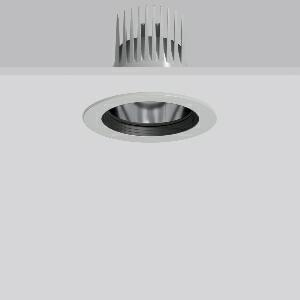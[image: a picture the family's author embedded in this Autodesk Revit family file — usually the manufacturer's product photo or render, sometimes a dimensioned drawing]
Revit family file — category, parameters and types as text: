
# Revit family: heledon_maxi_e_901764_004_3_76_aa6f
name_source: partatom
category: Lighting Fixtures
units: mm (PartAtom-declared; Revit-internal decimal feet)

## family parameters
Cut with Voids When Loaded = No
Host = Face
Light Source = No
Part Type = Normal
Room Calculation Point = No
Round Connector Dimension = Use Diameter
Shared = No

## types (1)
- HELEDON maxi E (1 x LED Modul 935, 4350 lm, 3500)
    Apparent Load = 35 VA
    Approval mark = CE
    CIE Flux Codes = 100 100 100 100 100
    Color Rendering = 92
    Color Temperature = 3500
    Default Elevation = 1800 mm
    Description = Series: HELEDON maxi
Round recessed downlight. Housing: die-cast aluminium, powder-coated. Black plastic ring and recessed LED to prevent glare from the side. Optical assembly with reflector made of MIRO-Silver with 98% total light reflection for outstanding efficiency - can be changed without tools. Best colour rendering index Ra>90. Suitable for Recessed ceiling mounting. Installation without tools thanks to spring fastening system. Including separate LED converter with connecting cable 600 mm.High quality converter without flickering and stroboscopic effect. Through-wiring box (5 pole) available as accessory. The following accessories can be mounted without use of tools: interchangeable lenses, decorative glasses, honeycomb louvre, clear and frosted diffusers, white interchangeable plastic ring. 
Colour: silver
Diameter: 162 mm
Height: 3 mm
Cut-out diameter: 152 mm
Recess height: 200 mm
Luminaire: recess height: 135 mm
Lamp: LED
Socket: without socket
Colour temperature: 3500K
Colour rendering index (CRI): 92
System power: 35 W
Rated luminous flux: 4350 lm
Luminous efficiency: 124 lm/W
Control gear: Converter, dimmable, DALI
Protection class: II
Type of protection: IP 20
    Height = 0 mm  [stored 0 ft]
    Lamp = 1 x LED Modul 935
    Lamp Light Flux = 4350 lm
    Lamp count = 1
    Length = 162 mm
    Lifetime = 50000 h
    Luminous efficacy = 124 lm/W
    Manufacturer = RZB
    ModVariant = No
    Model = 901764.004.3.76
    Mounting Place = Ceiling
    Mounting Type = Recessed
    Number of Poles = 1
    OnlyDefault = Yes
    Power Factor = 1
    Product Name = HELEDON maxi E
    Product group = Recessed downlights
    ProductGroupID = 402
    Protection Class = Protection class II
    Protection Degree = IP 20
    RLX_Detail_Level = 1
    RLX_Emergency_Light_Flux = 0 lm
    RLX_Emergency_Type = 0
    RLX_Emergency_Type_DB = No
    RlxData = <blob elided: 119553 chars, md5=b64f9aeb>
    Socket = socket
    Standby Power = 0 W
    System Light Flux = 4350 lm
    System Power = 35 W
    Type Comments = Product without accessories
    Type Image = 901662.004.jpg
    URL = http://relux.com
    VarID = ---
    Voltage = 230 V
    Voltage Range = 220-240 V
    Weight = 0.00 kg
    Width = 0 mm  [stored 0 ft]

note: [stored X ft] marks values corroborated as IEEE doubles in the binary element streams (Revit-internal decimal feet)

## geometry (parser evidence)
native form markers: Blend x4, Sweep x11
no freeform markers — native parametric forms only
